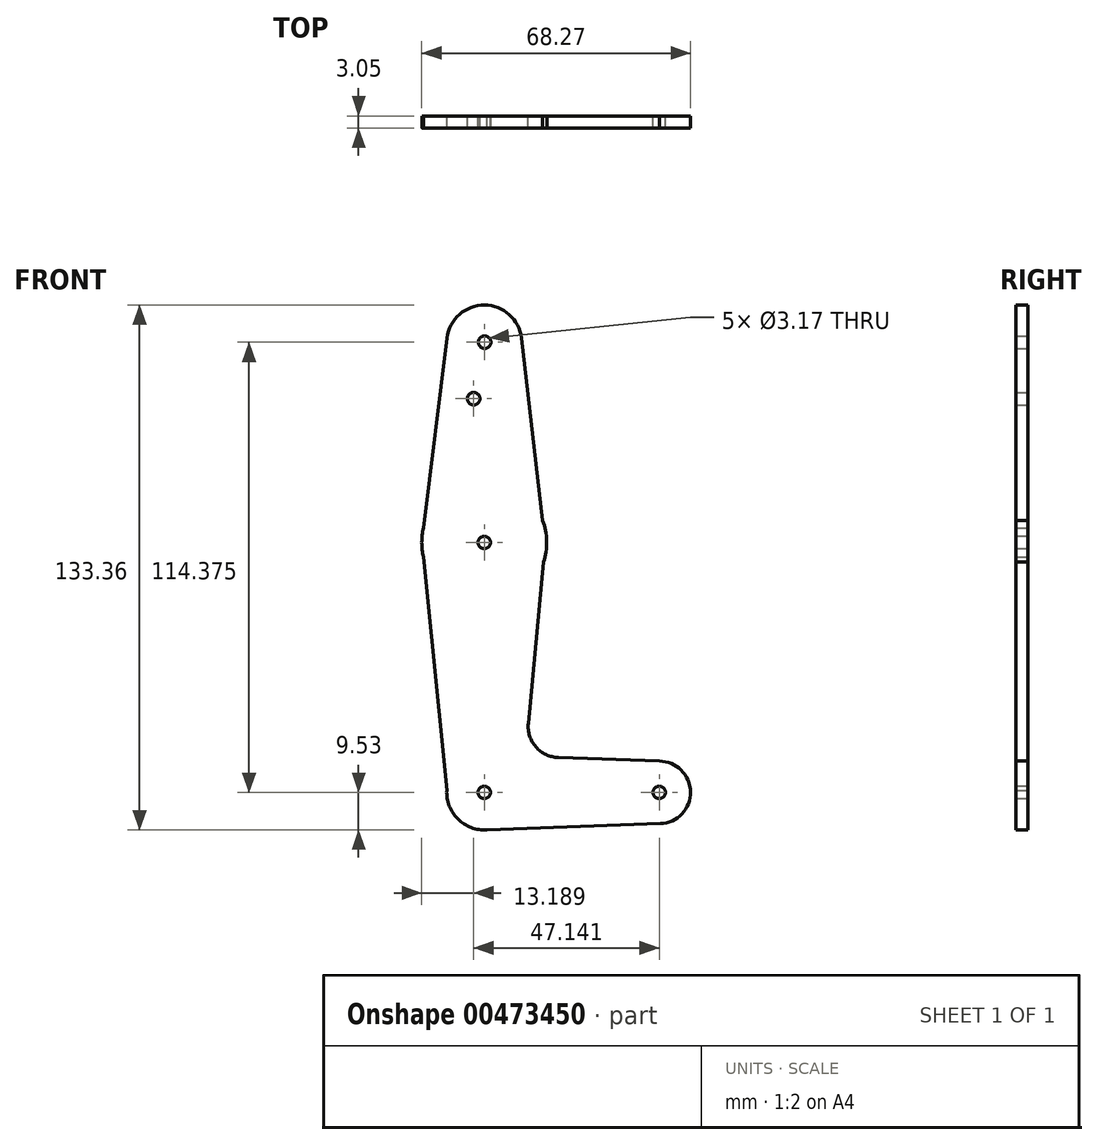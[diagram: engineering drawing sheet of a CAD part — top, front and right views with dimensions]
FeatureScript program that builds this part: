
annotation { "Feature Type Name" : "Feature", "Feature Type Description" : "" }
export const myFeature = defineFeature(function(context is Context, id is Id, definition is map)
    precondition{}
    {
        {
            var Q0;
            Q0=qCreatedBy(makeId("Front.planeOp"),FACE);
            var sketch = newSketch(context, id + "F0", { "sketchPlane" : qUnion([Q0])});
            skCircle(sketch, "E0", {"center": v(0, 0) * mm, "radius": 9.53 * mm});
            skCircle(sketch, "E1", {"center": v(0, 63.5) * mm, "radius": 15.88 * mm});
            skCircle(sketch, "E2", {"center": v(0, 114.3) * mm, "radius": 9.53 * mm});
            skCircle(sketch, "E3", {"center": v(44.45, 0) * mm, "radius": 7.94 * mm});
            skLineSegment(sketch, "E4", {"start": v(44.45, 0) * mm, "end": v(0, 0) * mm, "construction": true});
            skLineSegment(sketch, "E5", {"start": v(0, 0) * mm, "end": v(0, 63.5) * mm});
            skLineSegment(sketch, "E6", {"start": v(0, 114.3) * mm, "end": v(0, 0) * mm, "construction": true});
            skLineSegment(sketch, "E7", {"start": v(-15.44, 67.19) * mm, "end": v(-9.45, 115.47) * mm});
            skLineSegment(sketch, "E8", {"start": v(-15.44, 59.81) * mm, "end": v(-9.45, 0) * mm});
            skLineSegment(sketch, "E9", {"start": v(11.19, 17.55) * mm, "end": v(15.06, 58.5) * mm});
            skLineSegment(sketch, "E10", {"start": v(15.06, 67.19) * mm, "end": v(9.45, 115.47) * mm});
            skLineSegment(sketch, "E11", {"start": v(18.82, 8.85) * mm, "end": v(44.45, 7.94) * mm});
            skLineSegment(sketch, "E12", {"start": v(0, -9.53) * mm, "end": v(44.73, -7.93) * mm});
            skArc(sketch, "E13.filletArc", {"start": v(11.19, 17.55) * mm, "mid": v(13.13, 11.55) * mm, "end": v(18.82, 8.85) * mm});
            skCircle(sketch, "E14", {"center": v(-2.7, 100.03) * mm, "radius": 1.59 * mm});
            skCircle(sketch, "E15", {"center": v(0, 0) * mm, "radius": 1.59 * mm});
            skCircle(sketch, "E16", {"center": v(44.45, 0) * mm, "radius": 1.59 * mm});
            skCircle(sketch, "E17", {"center": v(0.11, 114.37) * mm, "radius": 1.59 * mm});
            skCircle(sketch, "E18", {"center": v(0, 63.5) * mm, "radius": 1.59 * mm});
            skLineSegment(sketch, "E19", {"start": v(0, 63.5) * mm, "end": v(0, 100.03) * mm});
            skSolve(sketch);
        }
        {
            var Q0;
            Q0 = qSketchRegion(id + "F0", true);
            extrude(context, id + "F1", {"entities" : qUnion([Q0]), "depth" : 3.05 * mm});
        }
    });
